# Revit family: REGA 50 SUSP PLAF
name_source: partatom
category: Luminaires
units: mm (PartAtom-declared; Revit-internal decimal feet)

## family parameters
Cote de connecteur circulaire = Utiliser le diamètre
Couper avec des vides une fois chargée = Oui
Hôte = Face
Partagée = Non
Point de calcul de pièce = Oui
Source d'éclairage = Oui
Type d'élément = Normal

## types (3) — shared parameters
Angle de l'inclinaison = 60.00°
Elévation par défaut = 1219 mm
Emettre à partir de la longueur de la ligne = 610 mm
Fabricant = Resistex
Filtre de couleur = 16777215
Garantie = 5 ans
Gradation des changements de température de couleur de lampe = <Aucun>
IK = IK 07
IP = IP 40
Image du type = <Aucun>
Tension = 230 V
URL = https://www.resistex-sa.com
hauteur = 75 mm
indice de charge = Eclairage
largeur = 50 mm  [stored 0.164042 ft]
longueur = 1000 mm  [stored 3.28084 ft]
nbr poles = 1

## per-type parameters (varying)
| type | Charge apparente | Commentaires relatifs à la puissance | Description | Fichier de distribution photométrique | Modèle |
| 727006 | 49 VA | 27.9 | Luminaire ligne continue sur mesure, longueur adaptée au projet
Luminaire lineaire équipé de LEDs SMD
IP 40, IK 07
Larg. 50mm x Long. 1000mm x Haut. 75mm
Flux restitué 2337lm
Conso. système 27.9W
Efficacité lumineuse produit complet 83.7lm/W
LM80 L90F10 à 72000h (25°C)
SVM <.09
PstLM <1
Diffuseur Polycarbonate Direct/Symétrique Opalescent, Corps en Aluminium extrudé
IRC >80
Garantie 5 ans
Empreinte carbone 2.51gCO2/h
Indice de réparabilité 9,1 | REGA_727006_LD.ies | REGA 50 SUSP PLAF |
| 727007 | 51 VA | 29.1 | Luminaire ligne continue sur mesure, longueur adaptée au projet
Luminaire lineaire équipé de LEDs SMD
IP 40, IK 07
Larg. 50mm x Long. 1000mm x Haut. 75mm
Flux restitué 2434lm
Conso. système 29.1W
Efficacité lumineuse produit complet 83.6lm/W
LM80 L90F10 à 72000h (25°C)
SVM <0.9
PstLM <1
Diffuseur Polycarbonate Direct/Symétrique Opalescent, Corps en Aluminium extrudé
IRC 84
Garantie 5 ans
Empreinte carbone 2.61gCO2/h
Indice de réparabilité 9,1 | REGA_727007_LD.ies | REGA 50 SUSP PLAF |
| 727008 | 51 VA | 29.21 | Luminaire ligne continue sur mesure, longueur adaptée au projet
Luminaire lineaire équipé de LEDs SMD
IP 40, IK 07
Larg. 50mm x Long. 1000mm x Haut. 75mm
Flux restitué 2434lm à 4000K
Conso. système 29.1W
Efficacité lumineuse produit complet 83.6lm/W
LM80 L90F10 à 72000h (25°C)
SVM <0.9
PstLM <1
Diffuseur Polycarbonate Direct/Symétrique Opalescent, Corps en Aluminium extrudé
IRC 84 à 4000K
Garantie 5 ans
Empreinte carbone 2.61gCO2/h
Indice de réparabilité 9,1 | REGA_727008_LD.ies | REGA 50 SUSP PLAF TUNABLE WHITE |

note: [stored X ft] marks values corroborated as IEEE doubles in the binary element streams (Revit-internal decimal feet)
